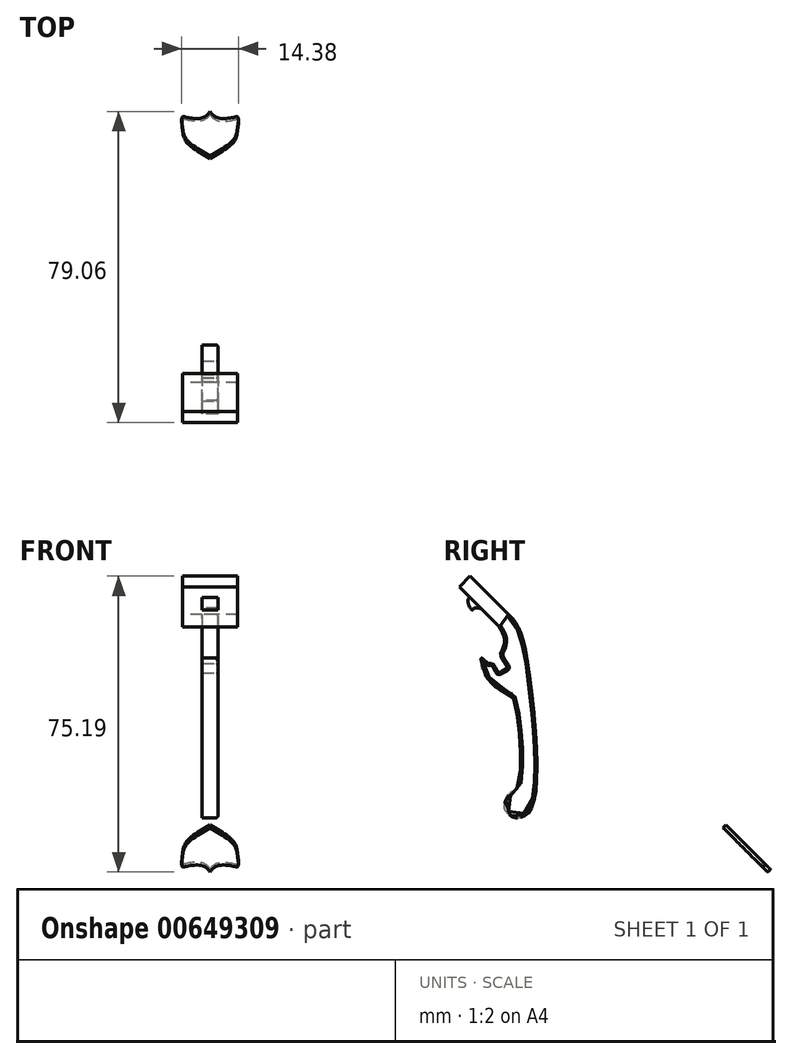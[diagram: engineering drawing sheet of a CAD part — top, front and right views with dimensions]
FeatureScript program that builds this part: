
annotation { "Feature Type Name" : "Feature", "Feature Type Description" : "" }
export const myFeature = defineFeature(function(context is Context, id is Id, definition is map)
    precondition{}
    {
        {
            var Q0;
            Q0=qCreatedBy(makeId("Right.planeOp"),FACE);
            var sketch = newSketch(context, id + "F0", { "sketchPlane" : qUnion([Q0])});
            skLineSegment(sketch, "E0", {"start": v(-13.14, 53.55) * mm, "end": v(-13.14, 0) * mm, "construction": true});
            skFitSpline(sketch, "E1", {"points": [v(0.48, 1.59) * mm, v(1, 24.8) * mm, v(-1.58, 43.22) * mm, v(-4, 48.97) * mm, v(-8.33, 52.8) * mm, v(-14.4, 55.47) * mm, v(-15.66, 54.47) * mm, v(-15.5, 52.8) * mm, v(-14.57, 51.72) * mm, v(-14.16, 52.13) * mm, v(-11.66, 51.55) * mm, v(-7.74, 47.3) * mm, v(-6.5, 43.72) * mm, v(-7.08, 41.55) * mm, v(-7.5, 40.72) * mm, v(-7.4, 39.97) * mm, v(-6.74, 38.64) * mm, v(-6, 37.55) * mm, v(-5.74, 36.97) * mm, v(-7.24, 36.14) * mm, v(-8, 35.72) * mm, v(-8.9, 37.47) * mm, v(-9.66, 38.05) * mm, v(-10.74, 38.22) * mm, v(-12.33, 39.47) * mm, v(-12.5, 38.1) * mm, v(-12.12, 36.3) * mm, v(-9.6, 32.98) * mm, v(-7.76, 31.64) * mm, v(-6.12, 31.3) * mm, v(-4.24, 29.4) * mm, v(-3.1, 6.72) * mm, v(-4.88, 5.33) * mm, v(-6.47, 2.41) * mm, v(-6.47, 1.02) * mm, v(-4.69, -0.76) * mm, v(-2.5, -0.96) * mm, v(0.48, 1.59) * mm]});
            skSolve(sketch);
        }
        {
            var Q0;
            Q0 = qSketchRegion(id + "F0", true);
            extrude(context, id + "F1", {"entities" : qUnion([Q0]), "depth" : 2 * mm, "offsetDistance" : 25.4 * mm, "hasSecondDirection" : true, "secondDirectionOppositeDirection" : true, "secondDirectionDepth" : 2 * mm});
        }
        {
            var Q0;
            Q0=makeQuery(id+"F1.opExtrude","CAP_FACE",FACE,{"disambiguationData":[OSD([sQuery(id+"F0.wireOp",EDGE,"E1")])],"isStart":false});
            var sketch = newSketch(context, id + "F2", { "sketchPlane" : qUnion([Q0])});
            skLineSegment(sketch, "E2", {"start": v(-5.44, 50.6) * mm, "end": v(-15.2, 60.3) * mm});
            skLineSegment(sketch, "E3", {"start": v(-17.98, 57.5) * mm, "end": v(-15.2, 60.3) * mm});
            skLineSegment(sketch, "E4", {"start": v(-17.98, 57.5) * mm, "end": v(-7.78, 47.36) * mm});
            skLineSegment(sketch, "E5", {"start": v(-7.78, 47.36) * mm, "end": v(-5.44, 50.6) * mm});
            skSolve(sketch);
        }
        {
            var Q0;
            Q0 = qSketchRegion(id + "F2", true);
            extrude(context, id + "F3", {"entities" : qUnion([Q0]), "operationType" : NewBodyOperationType.ADD, "depth" : 5 * mm, "offsetDistance" : 25.4 * mm, "hasSecondDirection" : true, "secondDirectionOppositeDirection" : true, "secondDirectionDepth" : 9 * mm});
        }
        {
            var Q0;
            Q0=makeQuery(id+"F3.opExtrude","SWEPT_FACE",FACE,{"disambiguationData":[OSD([sQuery(id+"F2.wireOp",EDGE,"E2")])]});
            var sketch = newSketch(context, id + "F4", { "sketchPlane" : qUnion([Q0])});
            skPoint(sketch, "E6.7.internal.snap0", {"position": v(0, -53.3) * mm});
            skFitSpline(sketch, "E6", {"points": [v(0, -53.3) * mm, v(1.46, -51.32) * mm, v(3.67, -50.78) * mm, v(6.21, -51.3) * mm, v(7, -51.43) * mm, v(7, -47.8) * mm, v(5.8, -43) * mm, v(0, -37.35) * mm], "startDerivative": vector(9.63, 19.73) * mm, "endDerivative": vector(-30.28, 25.94) * mm});
            skFitSpline(sketch, "E7.MirrorCS", {"points": [v(0, -53.3) * mm, v(-1.46, -51.32) * mm, v(-3.67, -50.78) * mm, v(-6.21, -51.3) * mm, v(-7, -51.43) * mm, v(-7, -47.8) * mm, v(-5.8, -43) * mm, v(0, -37.35) * mm], "startDerivative": vector(-9.63, 19.73) * mm, "endDerivative": vector(30.28, 25.94) * mm});
            skSolve(sketch);
        }
        {
            var Q0;
            Q0 = qSketchRegion(id + "F4", true);
            extrude(context, id + "F5", {"entities" : qUnion([Q0]), "operationType" : NewBodyOperationType.ADD, "depth" : 1 * mm, "offsetDistance" : 25.4 * mm});
        }
        {
            var Q0;
            {var subQ0=sQuery(id+"F0.wireOp",EDGE,"E1");Q0=makeQuery(id+"F3.boolean.opBoolean","SPLIT",EDGE,{"disambiguationData":[TD([makeQuery(id+"F1.opExtrude","SWEPT_FACE",FACE,{"disambiguationData":[OSD([subQ0])]}),makeQuery(id+"F1.opExtrude","CAP_FACE",FACE,{"disambiguationData":[OSD([subQ0])],"isStart":false}),makeQuery(id+"F3.opExtrude","SWEPT_FACE",FACE,{"disambiguationData":[OSD([sQuery(id+"F2.wireOp",EDGE,"E2")])]}),makeQuery(id+"F3.opExtrude","SWEPT_FACE",FACE,{"disambiguationData":[OSD([sQuery(id+"F2.wireOp",EDGE,"E4")])]}),makeQuery(id+"F3.opExtrude","SWEPT_FACE",FACE,{"disambiguationData":[OSD([sQuery(id+"F2.wireOp",EDGE,"E5")])]})])],"derivedFrom":makeQuery(id+"F1.opExtrude","CAP_EDGE",EDGE,{"disambiguationData":[OSD([subQ0])],"isStart":false})});}
            fillet(context, id + "F6", {"entities" : qUnion([Q0]), "radius" : 0.5 * mm, "tangentPropagation" : true, "allowEdgeOverflow" : false});
        }
    });
